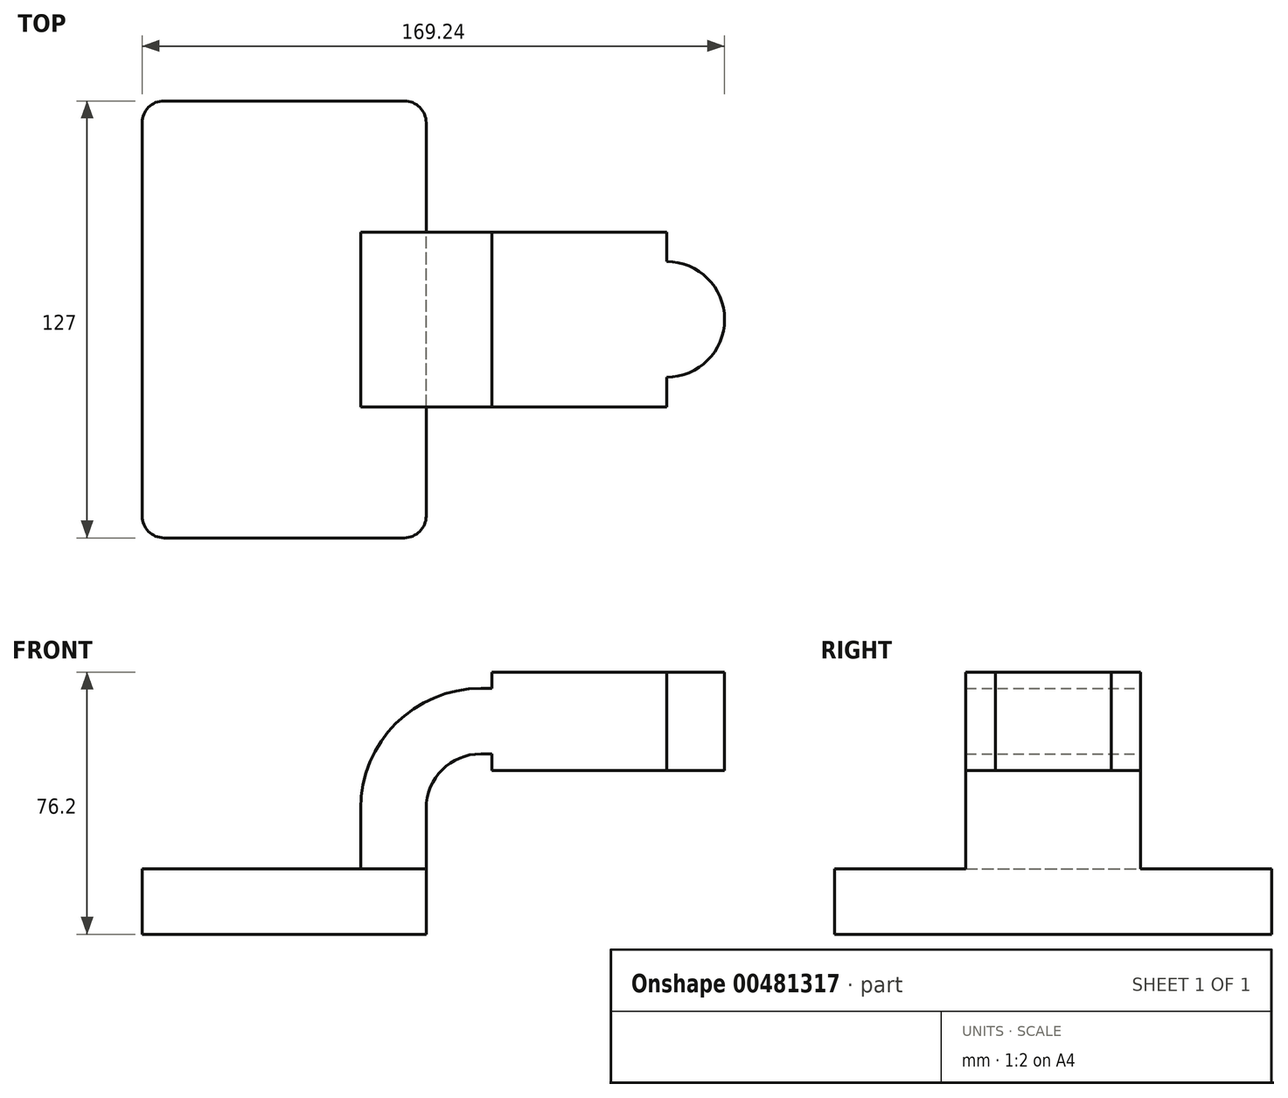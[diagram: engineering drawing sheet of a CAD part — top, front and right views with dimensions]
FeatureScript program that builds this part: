
annotation { "Feature Type Name" : "Feature", "Feature Type Description" : "" }
export const myFeature = defineFeature(function(context is Context, id is Id, definition is map)
    precondition{}
    {
        {
            var Q0;
            Q0=qCreatedBy(makeId("Front.planeOp"),FACE);
            var sketch = newSketch(context, id + "F0", { "sketchPlane" : qUnion([Q0])});
            skLineSegment(sketch, "E0.bottom", {"start": v(-41.28, -9.53) * mm, "end": v(41.28, -9.53) * mm});
            skLineSegment(sketch, "E0.top", {"start": v(-41.28, 9.53) * mm, "end": v(41.28, 9.53) * mm});
            skLineSegment(sketch, "E0.left", {"start": v(-41.28, -9.53) * mm, "end": v(-41.28, 9.53) * mm});
            skLineSegment(sketch, "E0.right", {"start": v(41.28, -9.53) * mm, "end": v(41.28, 9.53) * mm});
            skPoint(sketch, "E0.middle", {"position": v(0, 0) * mm});
            skLineSegment(sketch, "E1.bottom", {"start": v(111.12, 66.67) * mm, "end": v(60.32, 66.67) * mm});
            skLineSegment(sketch, "E1.top", {"start": v(111.12, 38.1) * mm, "end": v(60.33, 38.1) * mm});
            skLineSegment(sketch, "E1.left", {"start": v(111.12, 66.68) * mm, "end": v(111.12, 38.1) * mm});
            skLineSegment(sketch, "E1.right", {"start": v(60.32, 66.68) * mm, "end": v(60.33, 38.1) * mm});
            skLineSegment(sketch, "E2", {"start": v(41.27, 9.53) * mm, "end": v(41.27, 27) * mm});
            skArc(sketch, "E3", {"start": v(41.27, 27) * mm, "mid": v(45.92, 38.23) * mm, "end": v(57.15, 42.88) * mm});
            skLineSegment(sketch, "E4", {"start": v(57.15, 42.88) * mm, "end": v(94.28, 42.88) * mm});
            skLineSegment(sketch, "E5.0", {"start": v(57.15, 61.93) * mm, "end": v(94.28, 61.93) * mm});
            skArc(sketch, "E5.1", {"start": v(22.22, 27) * mm, "mid": v(32.45, 51.7) * mm, "end": v(57.15, 61.93) * mm});
            skLineSegment(sketch, "E5.2", {"start": v(22.22, 9.53) * mm, "end": v(22.22, 27) * mm});
            skLineSegment(sketch, "E6", {"start": v(94.28, 38.1) * mm, "end": v(94.28, 66.67) * mm});
            skFitSpline(sketch, "E7", {"points": [v(-41.28, 9.52) * mm, v(57.15, 61.93) * mm], "startDerivative": vector(66.7, 124.65) * mm, "endDerivative": vector(160.1, -1.35) * mm});
            skSolve(sketch);
        }
        {
            var Q0;
            Q0=makeQuery(id+"F0.imprint","IMPRINT",FACE,{"disambiguationData":[TD([[makeQuery(id+"F0.imprint","IMPRINT",EDGE,{"derivedFrom":sQuery(id+"F0.wireOp",EDGE,"E0.bottom")}),1.0]])]});
            extrude(context, id + "F1", {"entities" : qUnion([Q0]), "endBound" : BoundingType.SYMMETRIC, "depth" : 127 * mm});
        }
        {
            var Q0;
            Q0=makeQuery(id+"F0.imprint","IMPRINT",FACE,{"disambiguationData":[TD([[makeQuery(id+"F0.imprint","IMPRINT",EDGE,{"derivedFrom":sQuery(id+"F0.wireOp",EDGE,"E5.1")}),1.0]])]});
            extrude(context, id + "F2", {"entities" : qUnion([Q0]), "operationType" : NewBodyOperationType.ADD, "endBound" : BoundingType.SYMMETRIC, "depth" : 15.88 * mm});
        }
        {
            var Q0;
            {var subQ1=sQuery(id+"F0.wireOp",EDGE,"E2");Q0=makeQuery(id+"F0.imprint","IMPRINT",FACE,{"disambiguationData":[TD([[makeQuery(id+"F0.imprint","IMPRINT",EDGE,{"derivedFrom":subQ1}),1.0]])]});}
            var Q1;
            {var subQ0=sQuery(id+"F0.wireOp",EDGE,"E1.right");var subQ1=sQuery(id+"F0.wireOp",EDGE,"E1.top");var subQ2=makeQuery(id+"F0.imprint","INTERSECT",VERTEX,{"derivedFrom":[subQ1,subQ0]});Q1=makeQuery(id+"F0.imprint","IMPRINT",FACE,{"disambiguationData":[TD([[makeQuery(id+"F0.imprint","IMPRINT",EDGE,{"disambiguationData":[TD([[subQ2,1.0]])],"derivedFrom":subQ1}),-1.0]])]});}
            var Q2;
            {var subQ0=sQuery(id+"F0.wireOp",EDGE,"E5.0");var subQ1=sQuery(id+"F0.wireOp",EDGE,"E1.right");var subQ2=makeQuery(id+"F0.imprint","INTERSECT",VERTEX,{"derivedFrom":[subQ1,subQ0]});Q2=makeQuery(id+"F0.imprint","IMPRINT",FACE,{"disambiguationData":[TD([[makeQuery(id+"F0.imprint","IMPRINT",EDGE,{"disambiguationData":[TD([[subQ2,-1.0]])],"derivedFrom":subQ1}),1.0]])]});}
            var Q3;
            {var subQ0=sQuery(id+"F0.wireOp",EDGE,"E1.right");var subQ1=sQuery(id+"F0.wireOp",EDGE,"E1.bottom");var subQ2=makeQuery(id+"F0.imprint","INTERSECT",VERTEX,{"derivedFrom":[subQ1,subQ0]});Q3=makeQuery(id+"F0.imprint","IMPRINT",FACE,{"disambiguationData":[TD([[makeQuery(id+"F0.imprint","IMPRINT",EDGE,{"disambiguationData":[TD([[subQ2,1.0]])],"derivedFrom":subQ1}),1.0]])]});}
            var Q4;
            {var subQ4=sQuery(id+"F0.wireOp",EDGE,"E1.left");Q4=makeQuery(id+"F0.imprint","IMPRINT",FACE,{"disambiguationData":[TD([[makeQuery(id+"F0.imprint","IMPRINT",EDGE,{"derivedFrom":subQ4}),-1.0]])]});}
            extrude(context, id + "F3", {"entities" : qUnion([Q0, Q1, Q2, Q3, Q4]), "operationType" : NewBodyOperationType.ADD, "endBound" : BoundingType.SYMMETRIC, "depth" : 50.8 * mm});
        }
        {
            var Q0;
            {var subQ4=sQuery(id+"F0.wireOp",EDGE,"E1.left");Q0=makeQuery(id+"F0.imprint","IMPRINT",FACE,{"disambiguationData":[TD([[makeQuery(id+"F0.imprint","IMPRINT",EDGE,{"derivedFrom":subQ4}),-1.0]])]});}
            var Q1;
            Q1=sQuery(id+"F0.wireOp",EDGE,"E1.left");
            revolve(context, id + "F4", {"operationType" : NewBodyOperationType.ADD, "entities" : qUnion([Q0]), "axis" : qUnion([Q1]), "revolveType" : RevolveType.FULL});
        }
        {
            var Q0;
            Q0=makeQuery(id+"F1.opExtrude","CAP_EDGE",EDGE,{"disambiguationData":[OSD([sQuery(id+"F0.wireOp",EDGE,"E0.left")])],"isStart":true});
            var Q1;
            Q1=makeQuery(id+"F1.opExtrude","CAP_EDGE",EDGE,{"disambiguationData":[OSD([sQuery(id+"F0.wireOp",EDGE,"E0.left")])],"isStart":false});
            var Q2;
            Q2=makeQuery(id+"F1.opExtrude","CAP_EDGE",EDGE,{"disambiguationData":[OSD([sQuery(id+"F0.wireOp",EDGE,"E0.right")])],"isStart":false});
            var Q3;
            Q3=makeQuery(id+"F1.opExtrude","CAP_EDGE",EDGE,{"disambiguationData":[OSD([sQuery(id+"F0.wireOp",EDGE,"E0.right")])],"isStart":true});
            fillet(context, id + "F5", {"entities" : qUnion([Q0, Q1, Q2, Q3]), "radius" : 6.35 * mm, "tangentPropagation" : true, "allowEdgeOverflow" : false});
        }
    });
